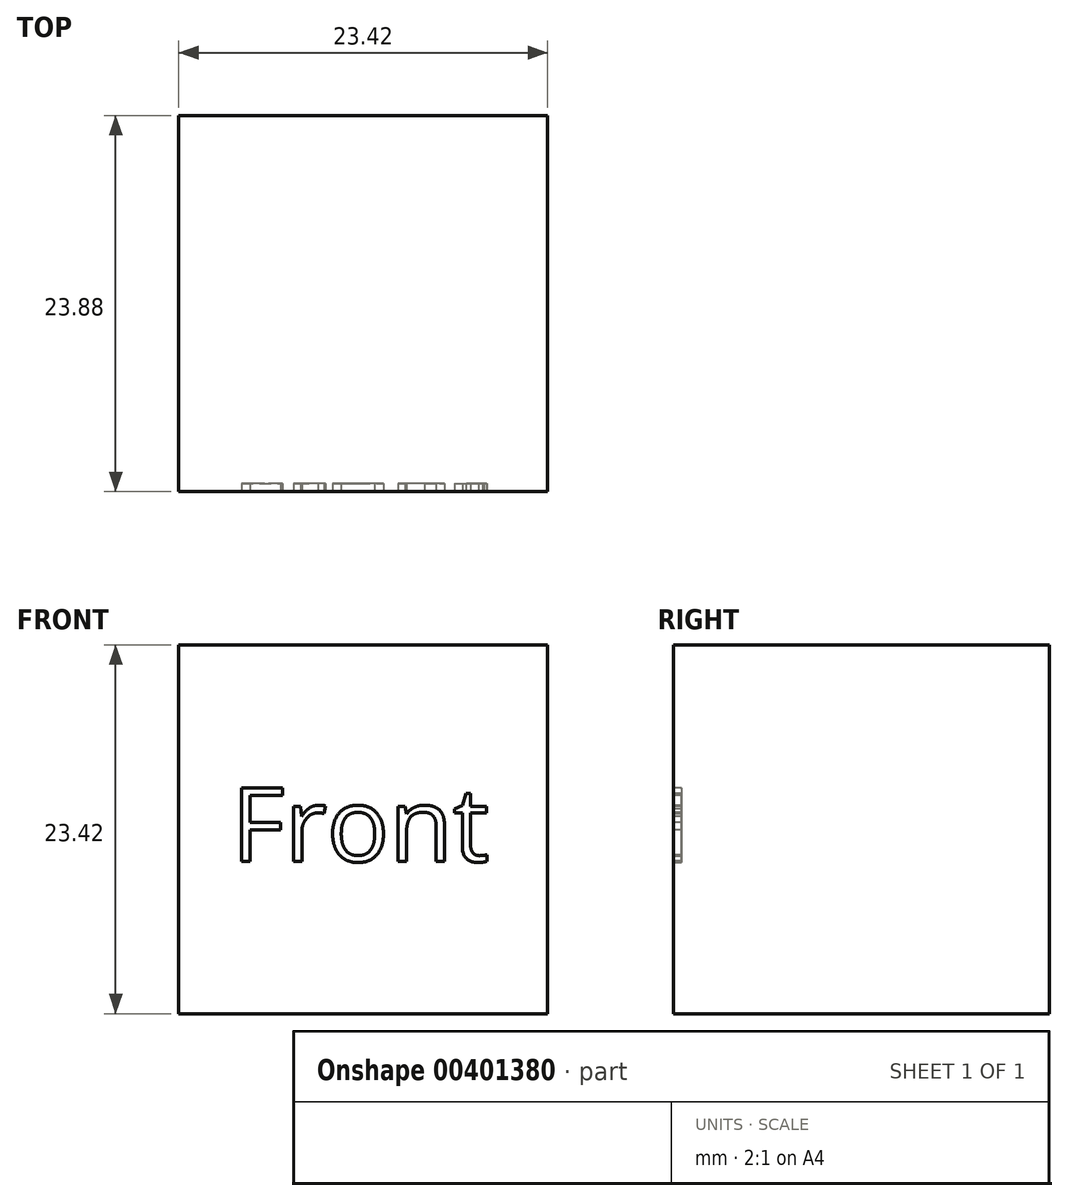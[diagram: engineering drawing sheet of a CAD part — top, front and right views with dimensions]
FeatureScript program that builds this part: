
annotation { "Feature Type Name" : "Feature", "Feature Type Description" : "" }
export const myFeature = defineFeature(function(context is Context, id is Id, definition is map)
    precondition{}
    {
        {
            var Q0;
            Q0=qCreatedBy(makeId("Front.planeOp"),FACE);
            var sketch = newSketch(context, id + "F0", { "sketchPlane" : qUnion([Q0])});
            skLineSegment(sketch, "E0.bottom", {"start": v(11.7, -11.7) * mm, "end": v(-11.7, -11.7) * mm});
            skLineSegment(sketch, "E0.top", {"start": v(11.7, 11.7) * mm, "end": v(-11.7, 11.7) * mm});
            skLineSegment(sketch, "E0.left", {"start": v(11.7, -11.7) * mm, "end": v(11.7, 11.7) * mm});
            skLineSegment(sketch, "E0.right", {"start": v(-11.7, -11.7) * mm, "end": v(-11.7, 11.7) * mm});
            skPoint(sketch, "E0.middle", {"position": v(0, 0) * mm});
            skSolve(sketch);
        }
        {
            var Q0;
            Q0 = qSketchRegion(id + "F0", true);
            extrude(context, id + "F1", {"entities" : qUnion([Q0]), "depth" : 23.88 * mm});
        }
        {
            var Q0;
            Q0=makeQuery(id+"F1.opExtrude","CAP_FACE",FACE,{"disambiguationData":[OSD([sQuery(id+"F0.wireOp",EDGE,"E0.bottom"),sQuery(id+"F0.wireOp",EDGE,"E0.top"),sQuery(id+"F0.wireOp",EDGE,"E0.left"),sQuery(id+"F0.wireOp",EDGE,"E0.right")])],"isStart":false});
            var sketch = newSketch(context, id + "F2", { "sketchPlane" : qUnion([Q0])});
            skText(sketch, "E1", { "text": "Front", "fontName": "OpenSans-Regular.ttf"});
            const initialGuessF2  = {"E1": [-0.00838, -0.00205, 1, 0, 0.00473]};
            skSetInitialGuess(sketch, initialGuessF2);
            skSolve(sketch);
        }
        {
            var Q0;
            Q0 = qSketchRegion(id + "F2", true);
            extrude(context, id + "F3", {"entities" : qUnion([Q0]), "operationType" : NewBodyOperationType.REMOVE, "oppositeDirection" : true, "depth" : 0.5 * mm});
        }
    });
